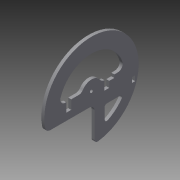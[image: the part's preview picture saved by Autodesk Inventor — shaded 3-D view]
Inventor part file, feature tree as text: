
AUTODESK INVENTOR PART (.ipt)
format: ipt  version: 2015 (Build 190159000, 159)  size: 174,592 bytes
history: native  units: mm
features: extrude x5, sketch x4
ambient origin geometry x8: Origin, YZ Plane, XZ Plane, XY Plane, X Axis, Y Axis, Z Axis, Center Point
bodies: Body1 (feature_tree)
feature tree (9):
  extrude  "Extrusion3"  Depth=32.0mm
  extrude  "Extrusion5"  Depth=3.0mm
  extrude  "Extrusion6"  Depth=3.0mm TaperAngle=0.0deg
  extrude  "Extrusion7"  Depth=40.0mm
  extrude  "Extrusion8"  Depth=8.0mm
  sketch  "Sketch2"  dims[d0=94.0mm d5=32.0mm]
  sketch  "Sketch4"  dims[d6=20.0mm d7=3.0mm]
  sketch  "Sketch5"  dims[d8=47.0mm d36=3.0mm d37=0.0mm]
  sketch  "Sketch6"  dims[d38=3.0mm d41=40.0mm d42=8.0mm d43=5.0mm d52=3.0mm d53=3.0mm d54=5.0mm d55=3.0mm d56=0.0mm d57=9.0mm d59=5.0mm d60=20.0mm d61=9.0mm d62=5.0mm d63=12.5mm d64=3.0mm d65=0.0mm d66=46.5mm d67=5.0mm d68=3.0mm d69=10.0mm d70=0.0mm d72=73.0mm d73=10.0mm d74=5.0mm d75=2.0mm d76=10.0mm d77=0.0mm d78=16.0mm d79=5.0mm d80=3.0mm d81=3.0mm d82=5.0mm]
